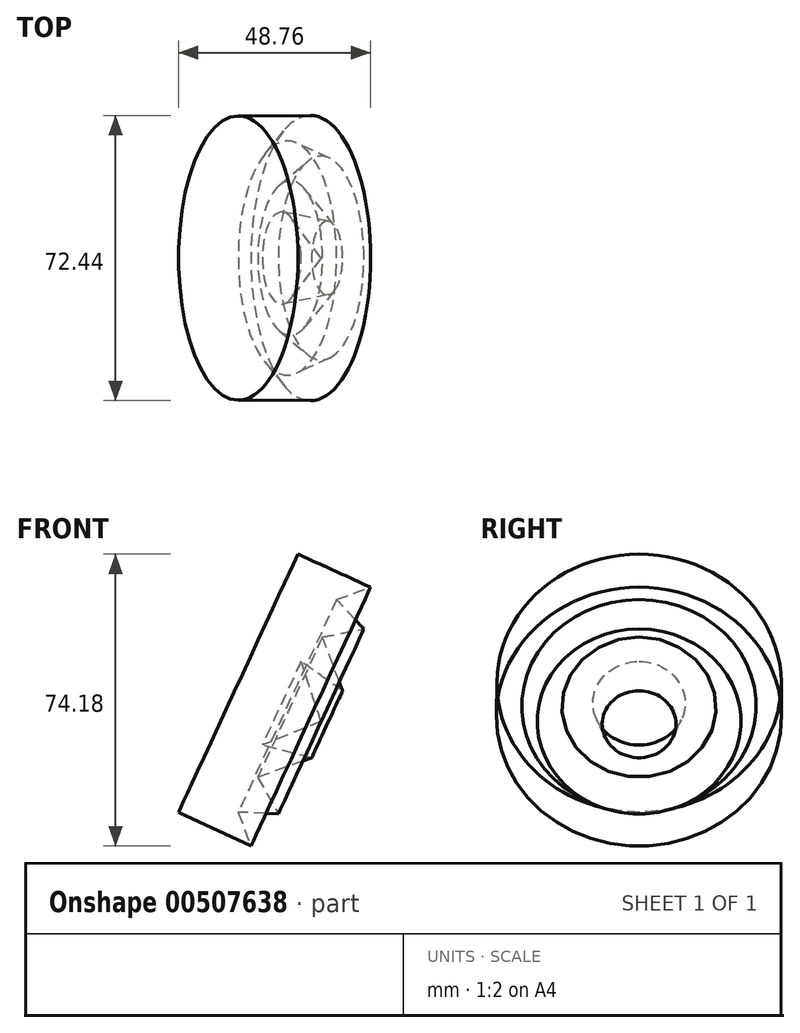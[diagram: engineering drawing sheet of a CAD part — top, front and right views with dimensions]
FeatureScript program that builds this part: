
annotation { "Feature Type Name" : "Feature", "Feature Type Description" : "" }
export const myFeature = defineFeature(function(context is Context, id is Id, definition is map)
    precondition{}
    {
        {
            var Q0;
            Q0=qCreatedBy(makeId("Front.planeOp"),FACE);
            var sketch = newSketch(context, id + "F0", { "sketchPlane" : qUnion([Q0])});
            skLineSegment(sketch, "E0", {"start": v(-41.39, 0) * mm, "end": v(-26.23, 32.8) * mm});
            skLineSegment(sketch, "E1", {"start": v(-26.23, 32.8) * mm, "end": v(-5.2, 23.07) * mm});
            skLineSegment(sketch, "E2", {"start": v(-5.2, 23.07) * mm, "end": v(-20.11, 17.05) * mm});
            skLineSegment(sketch, "E3", {"start": v(-20.11, 17.05) * mm, "end": v(-7.58, 13.85) * mm});
            skLineSegment(sketch, "E4", {"start": v(-7.58, 13.85) * mm, "end": v(-21.28, 8.9) * mm});
            skLineSegment(sketch, "E5", {"start": v(-21.28, 8.9) * mm, "end": v(-16.03, -0.44) * mm});
            skLineSegment(sketch, "E6", {"start": v(-16.03, -0.44) * mm, "end": v(-26.23, 0) * mm});
            skLineSegment(sketch, "E7", {"start": v(-26.23, 0) * mm, "end": v(-23.03, -8.6) * mm});
            skLineSegment(sketch, "E8", {"start": v(-41.39, 0) * mm, "end": v(-23.03, -8.6) * mm});
            skSolve(sketch);
        }
        {
            var Q0;
            Q0=makeQuery(id+"F0.imprint","IMPRINT",FACE,{"disambiguationData":[TD([[makeQuery(id+"F0.imprint","IMPRINT",EDGE,{"derivedFrom":sQuery(id+"F0.wireOp",EDGE,"E0")}),-1.0]])]});
            var Q1;
            Q1=sQuery(id+"F0.wireOp",EDGE,"E1");
            revolve(context, id + "F1", {"entities" : qUnion([Q0]), "axis" : qUnion([Q1]), "revolveType" : RevolveType.FULL});
        }
    });
